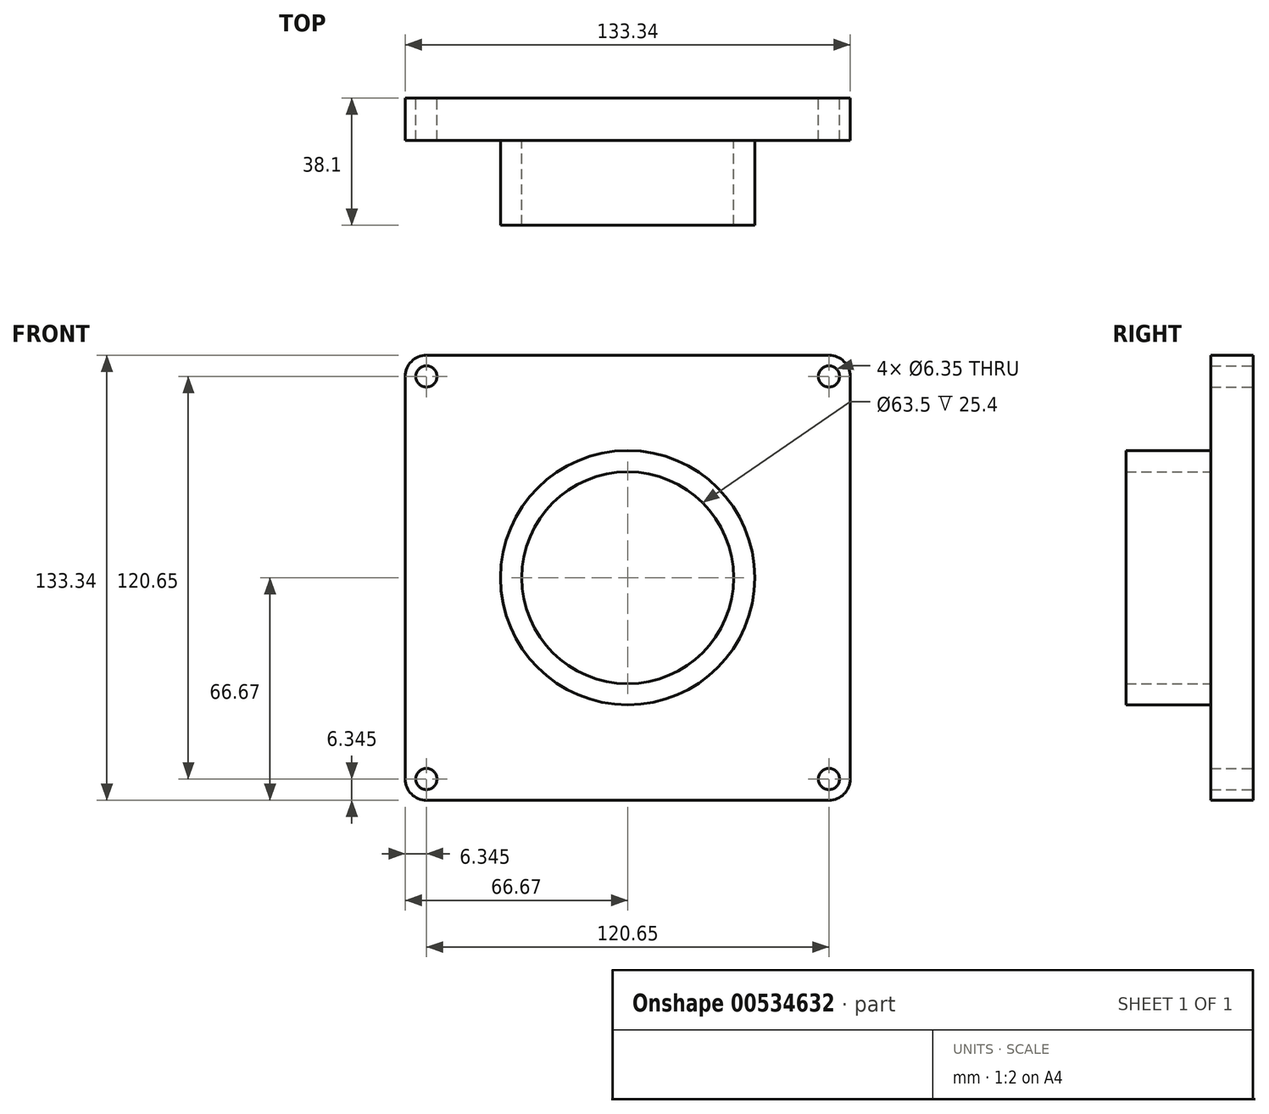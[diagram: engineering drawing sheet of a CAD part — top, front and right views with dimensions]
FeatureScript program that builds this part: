
annotation { "Feature Type Name" : "Feature", "Feature Type Description" : "" }
export const myFeature = defineFeature(function(context is Context, id is Id, definition is map)
    precondition{}
    {
        {
            var Q0;
            Q0=qCreatedBy(makeId("Front.planeOp"),FACE);
            var sketch = newSketch(context, id + "F0", { "sketchPlane" : qUnion([Q0])});
            skLineSegment(sketch, "E0.bottom", {"start": v(-60.33, 66.68) * mm, "end": v(60.32, 66.68) * mm});
            skLineSegment(sketch, "E0.top", {"start": v(-60.33, -66.68) * mm, "end": v(60.33, -66.68) * mm});
            skLineSegment(sketch, "E0.left", {"start": v(-66.68, 60.33) * mm, "end": v(-66.68, -60.33) * mm});
            skLineSegment(sketch, "E0.right", {"start": v(66.67, 60.33) * mm, "end": v(66.67, -60.33) * mm});
            skPoint(sketch, "E0.middle", {"position": v(0, 0) * mm});
            skPoint(sketch, "E1.visualSharp", {"position": v(-66.68, 66.68) * mm});
            skArc(sketch, "E1.filletArc", {"start": v(-60.33, 66.68) * mm, "mid": v(-64.82, 64.82) * mm, "end": v(-66.68, 60.33) * mm});
            skPoint(sketch, "E2.visualSharp", {"position": v(66.68, 66.68) * mm});
            skArc(sketch, "E2.filletArc", {"start": v(66.67, 60.33) * mm, "mid": v(64.82, 64.82) * mm, "end": v(60.32, 66.68) * mm});
            skPoint(sketch, "E3.visualSharp", {"position": v(-66.68, -66.68) * mm});
            skArc(sketch, "E3.filletArc", {"start": v(-66.68, -60.33) * mm, "mid": v(-64.82, -64.82) * mm, "end": v(-60.33, -66.68) * mm});
            skPoint(sketch, "E4.visualSharp", {"position": v(66.68, -66.68) * mm});
            skArc(sketch, "E4.filletArc", {"start": v(60.33, -66.68) * mm, "mid": v(64.82, -64.82) * mm, "end": v(66.68, -60.33) * mm});
            skCircle(sketch, "E5", {"center": v(-60.33, 60.33) * mm, "radius": 3.18 * mm});
            skCircle(sketch, "E6", {"center": v(60.32, 60.33) * mm, "radius": 3.18 * mm});
            skCircle(sketch, "E7", {"center": v(60.33, -60.33) * mm, "radius": 3.18 * mm});
            skCircle(sketch, "E8", {"center": v(-60.33, -60.33) * mm, "radius": 3.18 * mm});
            skSolve(sketch);
        }
        {
            var Q0;
            Q0=makeQuery(id+"F0.imprint","IMPRINT",FACE,{"disambiguationData":[TD([[makeQuery(id+"F0.imprint","IMPRINT",EDGE,{"derivedFrom":sQuery(id+"F0.wireOp",EDGE,"E0.bottom")}),-1.0]])]});
            extrude(context, id + "F1", {"entities" : qUnion([Q0]), "depth" : 12.7 * mm, "offsetDistance" : 25.4 * mm});
        }
        {
            var Q0;
            Q0=makeQuery(id+"F1.opExtrude","CAP_FACE",FACE,{"disambiguationData":[OSD([sQuery(id+"F0.wireOp",EDGE,"E0.bottom"),sQuery(id+"F0.wireOp",EDGE,"E0.top"),sQuery(id+"F0.wireOp",EDGE,"E0.left"),sQuery(id+"F0.wireOp",EDGE,"E0.right"),sQuery(id+"F0.wireOp",EDGE,"E1.filletArc"),sQuery(id+"F0.wireOp",EDGE,"E2.filletArc"),sQuery(id+"F0.wireOp",EDGE,"E3.filletArc"),sQuery(id+"F0.wireOp",EDGE,"E4.filletArc"),sQuery(id+"F0.wireOp",EDGE,"E5"),sQuery(id+"F0.wireOp",EDGE,"E6"),sQuery(id+"F0.wireOp",EDGE,"E7"),sQuery(id+"F0.wireOp",EDGE,"E8")])],"isStart":false});
            var sketch = newSketch(context, id + "F2", { "sketchPlane" : qUnion([Q0])});
            skCircle(sketch, "E9", {"center": v(0, 0) * mm, "radius": 38.1 * mm});
            skCircle(sketch, "E10", {"center": v(0, 0) * mm, "radius": 31.75 * mm});
            skSolve(sketch);
        }
        {
            var Q0;
            Q0=makeQuery(id+"F2.imprint","IMPRINT",FACE,{"disambiguationData":[TD([[makeQuery(id+"F2.imprint","IMPRINT",EDGE,{"derivedFrom":sQuery(id+"F2.wireOp",EDGE,"E10")}),-1.0]])]});
            extrude(context, id + "F3", {"entities" : qUnion([Q0]), "operationType" : NewBodyOperationType.ADD, "depth" : 25.4 * mm, "offsetDistance" : 25.4 * mm});
        }
    });
